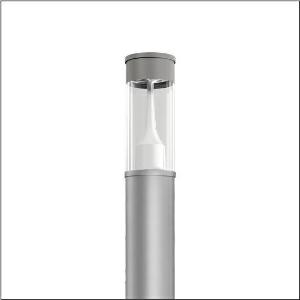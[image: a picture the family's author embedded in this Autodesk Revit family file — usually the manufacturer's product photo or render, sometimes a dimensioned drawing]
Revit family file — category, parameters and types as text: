
# Revit family: city-light_260_iq___pl1_2s_5xa5295rf14h_a018
name_source: partatom
category: Lighting Fixtures
units: mm (PartAtom-declared; Revit-internal decimal feet)

## family parameters
Cut with Voids When Loaded = No
Host = Face
Light Source = No
Part Type = Normal
Room Calculation Point = No
Round Connector Dimension = Use Diameter
Shared = No

## types (1)
- --- (1 x LED, 2970 lm, 18.5 W, 4000K)
    Apparent Load = 19 VA
    CIE Flux Codes = 23 62 94 96 100
    Color Rendering = 70
    Color Temperature = 4000K
    Default Elevation = 1800 mm
    Description = City-Light 260 iQ, light pillar, Module 540 iQ-SR, primary light control with 3 zone facetted reflector, of plastic, silver coated, highly specular, structured, primary optical cover: cover, of PMMA, transparent, partly coated, light distribution: PL1.2s, primary light characteristic: symmetric, LED, High Power LED, rated luminous flux: 2.970lm, luminous efficacy: 161lm/W, light colour: 740, colour temperature: 4000K, control gear: ECG iQ, control: presetting dimming logarithmic, Street-Remote, Auto-Match, Temp-Guard, Lumen-Switch, Night-Set, Smart-Wire, Light-Fading, Desk-Remote (wireless, voltage-free reading and setting of iQ features in the workshop via application-optimized NFC function/RFID function), optimised constant luminous flux control (CLO 2.0), with terminal, 6-pole, max. 2.5mm², mains connection: 230..240V, AC, 50/60Hz, start of lifetime: 19W, end of service life: 20W, reduction: 9W, luminaire housing, cylindrical, of extruded aluminium section, coated, Siteco® metallic grey (DB 702S), length: 2.600mm, diameter: 200mm, Module 540 iQ-SR, traffic white (RAL 9016), equipment: standard, protection rating (complete): IP65, insulation class (complete): insulation class II (safety insulation), certification: CE, ENEC, VDE, packaging unit: 1 piece

Light Distribution: PL1.2s
    Height = 500 mm
    Lamp = 1 x LED
    Lamp Light Flux = 2970 lm
    Lamp Power = 18.5 W
    Lamp count = 1
    Length = 200 mm  [stored 0.656168 ft]
    Luminous efficacy = 161 lm/W
    Manufacturer = Siteco
    ModVariant = No
    Model = 5XA5295RF14H
    Mounting Place = Floor
    Mounting Type = Freestanding
    Number of Poles = 1
    OnlyDefault = Yes
    Power Factor = 1
    Product Name = City-Light 260 iQ | PL1.2s
    Product group = light pillar
    ProductGroupID = 1303
    Protection Class = Protection class II
    Protection Degree = IP 65
    RLX_Detail_Level = 1
    RLX_Emergency_Light_Flux = 0 lm
    RLX_Emergency_Type = 0
    RLX_Emergency_Type_DB = No
    RlxData = <blob elided: 28869 chars, md5=59e52523>
    Socket = socket
    Standby Power = 0 W
    System Light Flux = 2970 lm
    System Power = 19 W
    Type Comments = factory setting: luminous flux: 100 % | dim-lin: 254 | 385 mA
    Type Image = l_1006920.jpg
    URL = http://relux.com
    VarID = @adj_094579
    Voltage = 0 V
    Weight = 0.00 kg
    Width = 0 mm  [stored 0 ft]

note: [stored X ft] marks values corroborated as IEEE doubles in the binary element streams (Revit-internal decimal feet)

## geometry (parser evidence)
native form markers: Blend x4, Sweep x11
no freeform markers — native parametric forms only
